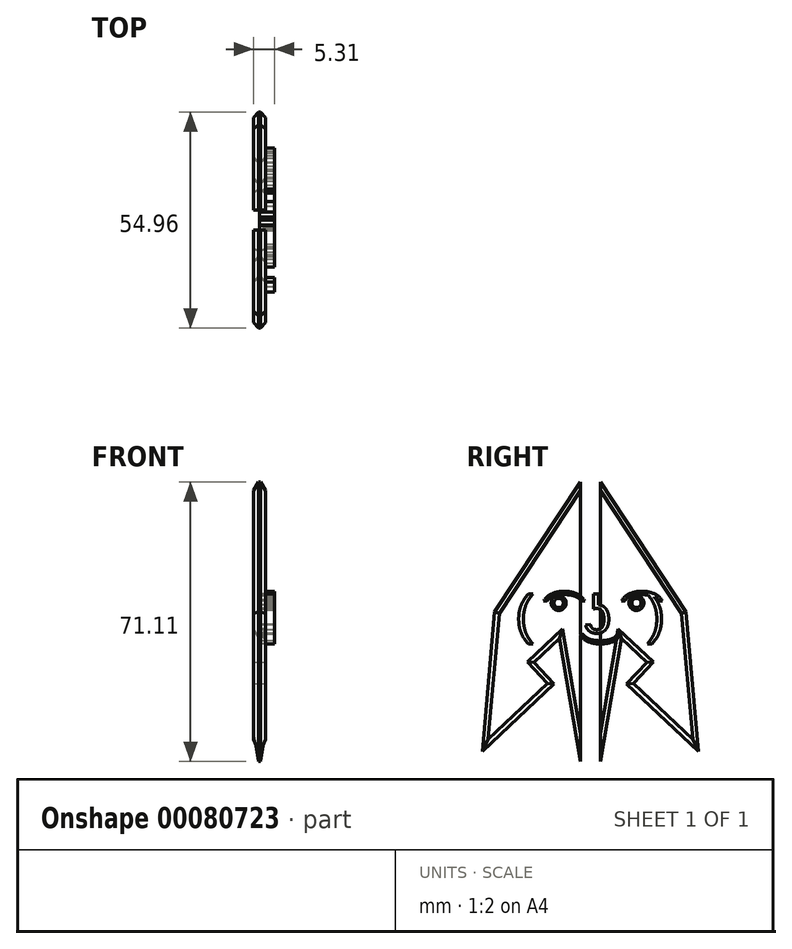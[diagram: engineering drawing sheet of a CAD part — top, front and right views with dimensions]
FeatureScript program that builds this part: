
annotation { "Feature Type Name" : "Feature", "Feature Type Description" : "" }
export const myFeature = defineFeature(function(context is Context, id is Id, definition is map)
    precondition{}
    {
        {
            var Q0;
            Q0=qCreatedBy(makeId("Front.planeOp"),FACE);
            var sketch = newSketch(context, id + "F0", { "sketchPlane" : qUnion([Q0])});
            skLineSegment(sketch, "E0", {"start": v(-7.53, 5.21) * mm, "end": v(9.93, 17.09) * mm});
            skLineSegment(sketch, "E1", {"start": v(9.93, 17.09) * mm, "end": v(37.87, 11.22) * mm});
            skLineSegment(sketch, "E2", {"start": v(37.87, 11.22) * mm, "end": v(24.89, -3.88) * mm});
            skLineSegment(sketch, "E3", {"start": v(24.89, -3.88) * mm, "end": v(36.76, -18.83) * mm});
            skLineSegment(sketch, "E4", {"start": v(36.76, -18.83) * mm, "end": v(17.76, -38.39) * mm});
            skLineSegment(sketch, "E5", {"start": v(17.76, -38.39) * mm, "end": v(-9.76, -32.52) * mm});
            skLineSegment(sketch, "E6", {"start": v(-9.76, -32.52) * mm, "end": v(-20.94, -11.7) * mm});
            skLineSegment(sketch, "E7", {"start": v(-20.94, -11.7) * mm, "end": v(-51.12, -5.28) * mm});
            skLineSegment(sketch, "E8", {"start": v(-51.12, -5.28) * mm, "end": v(-54.6, 16.24) * mm});
            skLineSegment(sketch, "E9", {"start": v(-54.6, 16.24) * mm, "end": v(-19.12, 33.56) * mm});
            skLineSegment(sketch, "E10", {"start": v(-19.12, 33.56) * mm, "end": v(-15.35, 7.3) * mm});
            skLineSegment(sketch, "E11", {"start": v(-15.35, 7.3) * mm, "end": v(0, -24.28) * mm});
            skLineSegment(sketch, "E12", {"start": v(0, -24.28) * mm, "end": v(17.61, -9.46) * mm});
            skLineSegment(sketch, "E13", {"start": v(17.61, -9.46) * mm, "end": v(-7.53, 5.21) * mm});
            skCircle(sketch, "E14", {"center": v(-34.49, 6.46) * mm, "radius": 11.12 * mm});
            skCircle(sketch, "E15", {"center": v(15.1, 6.74) * mm, "radius": 3.32 * mm});
            skCircle(sketch, "E16", {"center": v(15.53, -23.44) * mm, "radius": 4.35 * mm});
            skCircle(sketch, "E17", {"center": v(-34.49, 6.46) * mm, "radius": 4.66 * mm});
            skCircle(sketch, "E18", {"center": v(15.53, -23.44) * mm, "radius": 2.9 * mm});
            skCircle(sketch, "E19", {"center": v(15.1, 6.74) * mm, "radius": 2.18 * mm});
            skLineSegment(sketch, "E20", {"start": v(-34.02, 17.57) * mm, "end": v(-34.02, 11.1) * mm});
            skLineSegment(sketch, "E21", {"start": v(-36.93, 17.31) * mm, "end": v(-35.26, 11.06) * mm});
            skLineSegment(sketch, "E22", {"start": v(13.7, 9.75) * mm, "end": v(14.8, 8.9) * mm});
            skLineSegment(sketch, "E23", {"start": v(16.2, 9.88) * mm, "end": v(15.7, 8.83) * mm});
            skLineSegment(sketch, "E24", {"start": v(14.35, -20.8) * mm, "end": v(13.38, -19.65) * mm});
            skLineSegment(sketch, "E25", {"start": v(16.7, -20.8) * mm, "end": v(17.9, -19.8) * mm});
            skSolve(sketch);
        }
        {
            var Q0;
            Q0 = qSketchRegion(id + "F0", true);
            var Q1;
            {var subQ0=sQuery(id+"F0.wireOp",EDGE,"E20");Q1=makeQuery(id+"F0.imprint","IMPRINT",FACE,{"disambiguationData":[TD([[makeQuery(id+"F0.imprint","IMPRINT",EDGE,{"derivedFrom":subQ0}),-1.0]])]});}
            var Q2;
            {var subQ0=sQuery(id+"F0.wireOp",EDGE,"E17");var subQ1=makeQuery(id+"F0.imprint","INTERSECT",VERTEX,{"derivedFrom":[subQ0,sQuery(id+"F0.wireOp",EDGE,"E20")]});Q2=makeQuery(id+"F0.imprint","IMPRINT",FACE,{"disambiguationData":[TD([[makeQuery(id+"F0.imprint","IMPRINT",EDGE,{"disambiguationData":[TD([[subQ1,-1.0]])],"derivedFrom":subQ0}),1.0]])]});}
            var Q3;
            {var subQ0=sQuery(id+"F0.wireOp",EDGE,"E22");Q3=makeQuery(id+"F0.imprint","IMPRINT",FACE,{"disambiguationData":[TD([[makeQuery(id+"F0.imprint","IMPRINT",EDGE,{"derivedFrom":subQ0}),1.0]])]});}
            var Q4;
            {var subQ0=sQuery(id+"F0.wireOp",EDGE,"E19");var subQ1=makeQuery(id+"F0.imprint","INTERSECT",VERTEX,{"derivedFrom":[subQ0,sQuery(id+"F0.wireOp",EDGE,"E22")]});Q4=makeQuery(id+"F0.imprint","IMPRINT",FACE,{"disambiguationData":[TD([[makeQuery(id+"F0.imprint","IMPRINT",EDGE,{"disambiguationData":[TD([[subQ1,1.0]])],"derivedFrom":subQ0}),1.0]])]});}
            var Q5;
            {var subQ0=sQuery(id+"F0.wireOp",EDGE,"E24");Q5=makeQuery(id+"F0.imprint","IMPRINT",FACE,{"disambiguationData":[TD([[makeQuery(id+"F0.imprint","IMPRINT",EDGE,{"derivedFrom":subQ0}),-1.0]])]});}
            var Q6;
            {var subQ0=sQuery(id+"F0.wireOp",EDGE,"E18");var subQ1=makeQuery(id+"F0.imprint","INTERSECT",VERTEX,{"derivedFrom":[subQ0,sQuery(id+"F0.wireOp",EDGE,"E24")]});Q6=makeQuery(id+"F0.imprint","IMPRINT",FACE,{"disambiguationData":[TD([[makeQuery(id+"F0.imprint","IMPRINT",EDGE,{"disambiguationData":[TD([[subQ1,1.0]])],"derivedFrom":subQ0}),1.0]])]});}
            extrude(context, id + "F1", {"entities" : qUnion([Q0, Q1, Q2, Q3, Q4, Q5, Q6]), "endBound" : BoundingType.SYMMETRIC, "depth" : 5 * mm});
        }
        {
            var Q0;
            Q0=qCreatedBy(makeId("Right.planeOp"),FACE);
            var sketch = newSketch(context, id + "F2", { "sketchPlane" : qUnion([Q0])});
            skLineSegment(sketch, "E26", {"start": v(-24.32, 0) * mm, "end": v(-2.55, 33.07) * mm});
            skLineSegment(sketch, "E27", {"start": v(-24.32, 0) * mm, "end": v(-27.48, -35.38) * mm});
            skLineSegment(sketch, "E28", {"start": v(-27.48, -35.38) * mm, "end": v(-9.2, -18.27) * mm});
            skLineSegment(sketch, "E29", {"start": v(-9.2, -18.27) * mm, "end": v(-14.33, -12.79) * mm});
            skLineSegment(sketch, "E30", {"start": v(-14.33, -12.79) * mm, "end": v(-7.85, -6.72) * mm});
            skLineSegment(sketch, "E31", {"start": v(-7.85, -6.72) * mm, "end": v(-2.55, -38.04) * mm});
            skLineSegment(sketch, "E32", {"start": v(-2.55, 33.07) * mm, "end": v(-2.55, -38.04) * mm});
            skLineSegment(sketch, "E33.MirrorCS", {"start": v(24.32, 0) * mm, "end": v(2.55, 33.07) * mm});
            skLineSegment(sketch, "E34.MirrorCS", {"start": v(24.32, 0) * mm, "end": v(27.48, -35.38) * mm});
            skLineSegment(sketch, "E35.MirrorCS", {"start": v(14.33, -12.79) * mm, "end": v(7.85, -6.72) * mm});
            skLineSegment(sketch, "E36.MirrorCS", {"start": v(27.48, -35.38) * mm, "end": v(9.2, -18.27) * mm});
            skLineSegment(sketch, "E37.MirrorCS", {"start": v(9.2, -18.27) * mm, "end": v(14.33, -12.79) * mm});
            skLineSegment(sketch, "E38.MirrorCS", {"start": v(7.85, -6.72) * mm, "end": v(2.55, -38.04) * mm});
            skLineSegment(sketch, "E39.MirrorCS", {"start": v(2.55, 33.07) * mm, "end": v(2.55, -38.04) * mm});
            skSolve(sketch);
        }
        {
            var Q0;
            Q0=makeQuery(id+"F2.imprint","IMPRINT",FACE,{"disambiguationData":[TD([[makeQuery(id+"F2.imprint","IMPRINT",EDGE,{"derivedFrom":sQuery(id+"F2.wireOp",EDGE,"E26")}),-1.0]])]});
            var Q1;
            Q1=makeQuery(id+"F2.imprint","IMPRINT",FACE,{"disambiguationData":[TD([[makeQuery(id+"F2.imprint","IMPRINT",EDGE,{"derivedFrom":sQuery(id+"F2.wireOp",EDGE,"E33.MirrorCS")}),1.0]])]});
            extrude(context, id + "F3", {"entities" : qUnion([Q0, Q1]), "endBound" : BoundingType.SYMMETRIC, "depth" : 3 * mm});
        }
        {
            var Q0;
            Q0=makeQuery(id+"F3.opExtrude","CAP_EDGE",EDGE,{"disambiguationData":[OSD([sQuery(id+"F2.wireOp",EDGE,"E26")])],"isStart":false});
            var Q1;
            Q1=makeQuery(id+"F3.opExtrude","CAP_EDGE",EDGE,{"disambiguationData":[OSD([sQuery(id+"F2.wireOp",EDGE,"E27")])],"isStart":false});
            var Q2;
            Q2=makeQuery(id+"F3.opExtrude","CAP_EDGE",EDGE,{"disambiguationData":[OSD([sQuery(id+"F2.wireOp",EDGE,"E26")])],"isStart":true});
            var Q3;
            Q3=makeQuery(id+"F3.opExtrude","CAP_EDGE",EDGE,{"disambiguationData":[OSD([sQuery(id+"F2.wireOp",EDGE,"E27")])],"isStart":true});
            var Q4;
            Q4=makeQuery(id+"F3.opExtrude","CAP_EDGE",EDGE,{"disambiguationData":[OSD([sQuery(id+"F2.wireOp",EDGE,"E28")])],"isStart":true});
            var Q5;
            Q5=makeQuery(id+"F3.opExtrude","CAP_EDGE",EDGE,{"disambiguationData":[OSD([sQuery(id+"F2.wireOp",EDGE,"E28")])],"isStart":false});
            var Q6;
            Q6=makeQuery(id+"F3.opExtrude","CAP_EDGE",EDGE,{"disambiguationData":[OSD([sQuery(id+"F2.wireOp",EDGE,"E30")])],"isStart":true});
            var Q7;
            Q7=makeQuery(id+"F3.opExtrude","CAP_EDGE",EDGE,{"disambiguationData":[OSD([sQuery(id+"F2.wireOp",EDGE,"E31")])],"isStart":true});
            var Q8;
            Q8=makeQuery(id+"F3.opExtrude","CAP_EDGE",EDGE,{"disambiguationData":[OSD([sQuery(id+"F2.wireOp",EDGE,"E31")])],"isStart":false});
            var Q9;
            Q9=makeQuery(id+"F3.opExtrude","CAP_EDGE",EDGE,{"disambiguationData":[OSD([sQuery(id+"F2.wireOp",EDGE,"E30")])],"isStart":false});
            var Q10;
            Q10=makeQuery(id+"F3.opExtrude","CAP_EDGE",EDGE,{"disambiguationData":[OSD([sQuery(id+"F2.wireOp",EDGE,"E29")])],"isStart":true});
            var Q11;
            Q11=makeQuery(id+"F3.opExtrude","CAP_EDGE",EDGE,{"disambiguationData":[OSD([sQuery(id+"F2.wireOp",EDGE,"E29")])],"isStart":false});
            var Q12;
            Q12=makeQuery(id+"F3.opExtrude","CAP_EDGE",EDGE,{"disambiguationData":[OSD([sQuery(id+"F2.wireOp",EDGE,"E33.MirrorCS")])],"isStart":false});
            var Q13;
            Q13=makeQuery(id+"F3.opExtrude","CAP_EDGE",EDGE,{"disambiguationData":[OSD([sQuery(id+"F2.wireOp",EDGE,"E33.MirrorCS")])],"isStart":true});
            var Q14;
            Q14=makeQuery(id+"F3.opExtrude","CAP_EDGE",EDGE,{"disambiguationData":[OSD([sQuery(id+"F2.wireOp",EDGE,"E34.MirrorCS")])],"isStart":true});
            var Q15;
            Q15=makeQuery(id+"F3.opExtrude","CAP_EDGE",EDGE,{"disambiguationData":[OSD([sQuery(id+"F2.wireOp",EDGE,"E34.MirrorCS")])],"isStart":false});
            var Q16;
            Q16=makeQuery(id+"F3.opExtrude","CAP_EDGE",EDGE,{"disambiguationData":[OSD([sQuery(id+"F2.wireOp",EDGE,"E36.MirrorCS")])],"isStart":false});
            var Q17;
            Q17=makeQuery(id+"F3.opExtrude","CAP_EDGE",EDGE,{"disambiguationData":[OSD([sQuery(id+"F2.wireOp",EDGE,"E35.MirrorCS")])],"isStart":false});
            var Q18;
            Q18=makeQuery(id+"F3.opExtrude","CAP_EDGE",EDGE,{"disambiguationData":[OSD([sQuery(id+"F2.wireOp",EDGE,"E38.MirrorCS")])],"isStart":false});
            var Q19;
            Q19=makeQuery(id+"F3.opExtrude","CAP_EDGE",EDGE,{"disambiguationData":[OSD([sQuery(id+"F2.wireOp",EDGE,"E37.MirrorCS")])],"isStart":false});
            var Q20;
            Q20=makeQuery(id+"F3.opExtrude","CAP_EDGE",EDGE,{"disambiguationData":[OSD([sQuery(id+"F2.wireOp",EDGE,"E38.MirrorCS")])],"isStart":true});
            var Q21;
            Q21=makeQuery(id+"F3.opExtrude","CAP_EDGE",EDGE,{"disambiguationData":[OSD([sQuery(id+"F2.wireOp",EDGE,"E35.MirrorCS")])],"isStart":true});
            var Q22;
            Q22=makeQuery(id+"F3.opExtrude","CAP_EDGE",EDGE,{"disambiguationData":[OSD([sQuery(id+"F2.wireOp",EDGE,"E37.MirrorCS")])],"isStart":true});
            var Q23;
            Q23=makeQuery(id+"F3.opExtrude","CAP_EDGE",EDGE,{"disambiguationData":[OSD([sQuery(id+"F2.wireOp",EDGE,"E36.MirrorCS")])],"isStart":true});
            chamfer(context, id + "F4", {"entities" : qUnion([Q0, Q1, Q2, Q3, Q4, Q5, Q6, Q7, Q8, Q9, Q10, Q11, Q12, Q13, Q14, Q15, Q16, Q17, Q18, Q19, Q20, Q21, Q22, Q23]), "width" : 1.2 * mm, "tangentPropagation" : true});
        }
        {
            var Q0;
            Q0=makeQuery(id+"F1.opExtrude","CAP_EDGE",EDGE,{"disambiguationData":[OSD([sQuery(id+"F0.wireOp",EDGE,"E19")])],"isStart":true});
            var Q1;
            Q1=makeQuery(id+"F1.opExtrude","CAP_EDGE",EDGE,{"disambiguationData":[OSD([sQuery(id+"F0.wireOp",EDGE,"E19")])],"isStart":false});
            var Q2;
            Q2=makeQuery(id+"F1.opExtrude","CAP_EDGE",EDGE,{"disambiguationData":[OSD([sQuery(id+"F0.wireOp",EDGE,"E23")])],"isStart":false});
            var Q3;
            Q3=makeQuery(id+"F1.opExtrude","CAP_EDGE",EDGE,{"disambiguationData":[OSD([sQuery(id+"F0.wireOp",EDGE,"E22")])],"isStart":false});
            var Q4;
            Q4=makeQuery(id+"F1.opExtrude","CAP_EDGE",EDGE,{"disambiguationData":[OSD([sQuery(id+"F0.wireOp",EDGE,"E15")])],"isStart":false});
            var Q5;
            Q5=makeQuery(id+"F1.opExtrude","CAP_EDGE",EDGE,{"disambiguationData":[OSD([sQuery(id+"F0.wireOp",EDGE,"E23")])],"isStart":true});
            var Q6;
            Q6=makeQuery(id+"F1.opExtrude","CAP_EDGE",EDGE,{"disambiguationData":[OSD([sQuery(id+"F0.wireOp",EDGE,"E22")])],"isStart":true});
            var Q7;
            Q7=makeQuery(id+"F1.opExtrude","CAP_EDGE",EDGE,{"disambiguationData":[OSD([sQuery(id+"F0.wireOp",EDGE,"E15")])],"isStart":true});
            fillet(context, id + "F5", {"entities" : qUnion([Q0, Q1, Q2, Q3, Q4, Q5, Q6, Q7]), "radius" : .2 * mm, "tangentPropagation" : true, "allowEdgeOverflow" : false});
        }
        {
            var Q0;
            Q0=makeQuery(id+"F1.opExtrude","SWEPT_BODY",BODY,{"disambiguationData":[OSD([sQuery(id+"F0.wireOp",EDGE,"E0"),sQuery(id+"F0.wireOp",EDGE,"E1"),sQuery(id+"F0.wireOp",EDGE,"E2"),sQuery(id+"F0.wireOp",EDGE,"E3"),sQuery(id+"F0.wireOp",EDGE,"E4"),sQuery(id+"F0.wireOp",EDGE,"E5"),sQuery(id+"F0.wireOp",EDGE,"E6"),sQuery(id+"F0.wireOp",EDGE,"E7"),sQuery(id+"F0.wireOp",EDGE,"E8"),sQuery(id+"F0.wireOp",EDGE,"E9"),sQuery(id+"F0.wireOp",EDGE,"E10"),sQuery(id+"F0.wireOp",EDGE,"E11"),sQuery(id+"F0.wireOp",EDGE,"E12"),sQuery(id+"F0.wireOp",EDGE,"E13"),sQuery(id+"F0.wireOp",EDGE,"E14"),sQuery(id+"F0.wireOp",EDGE,"E15"),sQuery(id+"F0.wireOp",EDGE,"E16"),sQuery(id+"F0.wireOp",EDGE,"E17"),sQuery(id+"F0.wireOp",EDGE,"E18"),sQuery(id+"F0.wireOp",EDGE,"E19"),sQuery(id+"F0.wireOp",EDGE,"E20"),sQuery(id+"F0.wireOp",EDGE,"E21"),sQuery(id+"F0.wireOp",EDGE,"E22"),sQuery(id+"F0.wireOp",EDGE,"E23"),sQuery(id+"F0.wireOp",EDGE,"E24"),sQuery(id+"F0.wireOp",EDGE,"E25")])]});
            deleteBodies(context, id + "F6", {"entities" : qUnion([Q0])});
        }
        {
            var Q0;
            Q0=qCreatedBy(makeId("Right.planeOp"),FACE);
            var sketch = newSketch(context, id + "F7", { "sketchPlane" : qUnion([Q0])});
            skText(sketch, "E40", { "text": "( ͡° ͜ʖ ͡°)", "fontName": "Arimo-Regular.ttf"});
            const initialGuessF7  = {"E40": [-0.01906, -0.00532, 1, 0, 0.00977]};
            skSetInitialGuess(sketch, initialGuessF7);
            skSolve(sketch);
        }
        {
            var Q0;
            Q0 = qSketchRegion(id + "F7", true);
            extrude(context, id + "F8", {"entities" : qUnion([Q0]), "operationType" : NewBodyOperationType.ADD, "depth" : 3.8 * mm});
        }
    });
